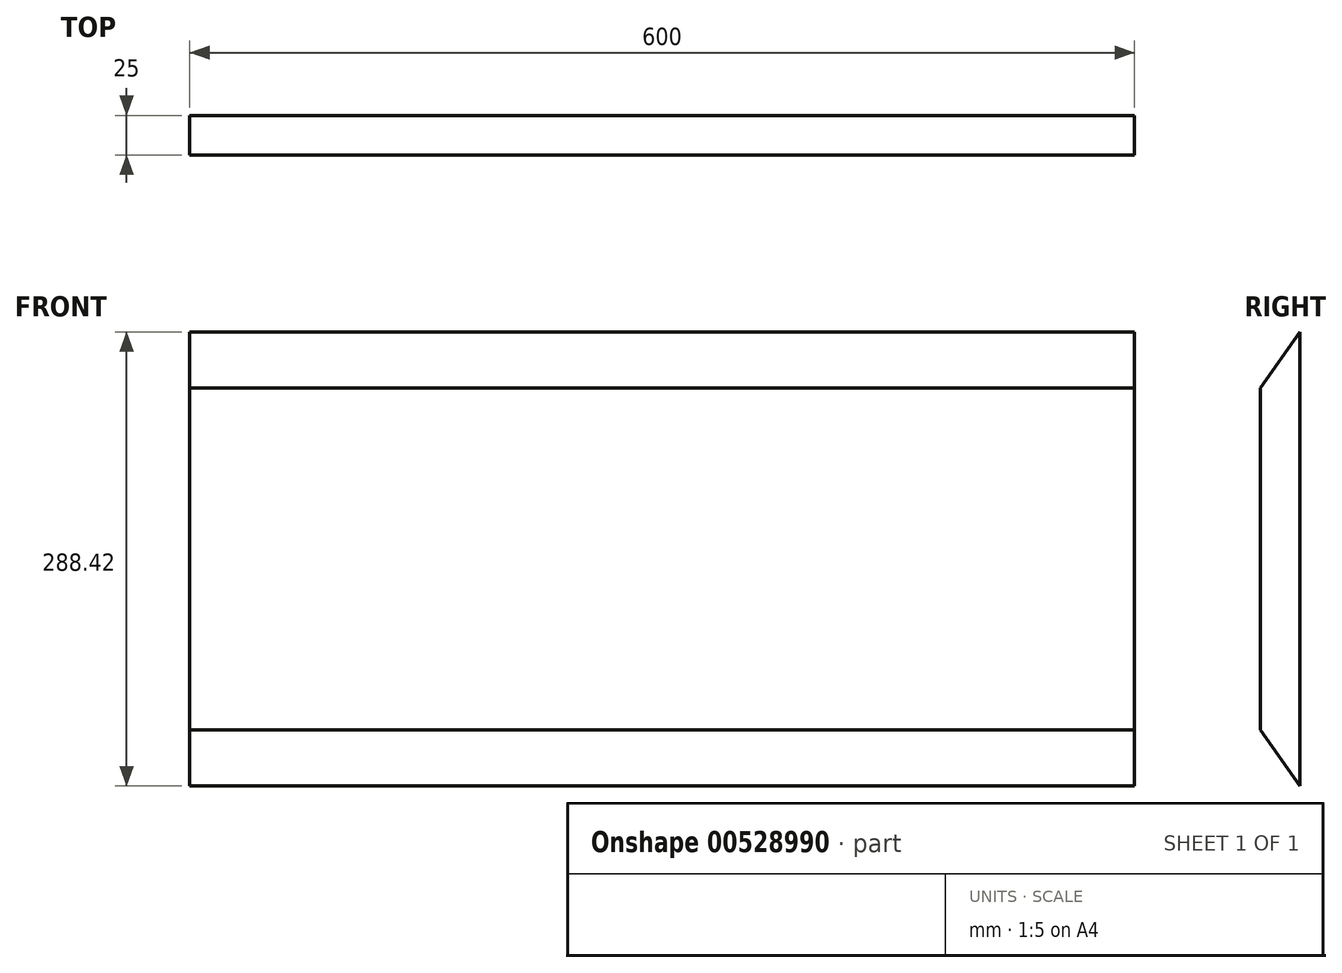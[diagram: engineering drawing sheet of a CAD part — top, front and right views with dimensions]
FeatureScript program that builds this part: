
annotation { "Feature Type Name" : "Feature", "Feature Type Description" : "" }
export const myFeature = defineFeature(function(context is Context, id is Id, definition is map)
    precondition{}
    {
        {
            var Q0;
            Q0=qCreatedBy(makeId("Right.planeOp"),FACE);
            var sketch = newSketch(context, id + "F0", { "sketchPlane" : qUnion([Q0])});
            skLineSegment(sketch, "E0", {"start": v(0, 84.61) * mm, "end": v(0, -203.8) * mm});
            skLineSegment(sketch, "E1", {"start": v(0, -203.8) * mm, "end": v(-25, -168.1) * mm});
            skLineSegment(sketch, "E2", {"start": v(-25, -168.1) * mm, "end": v(-25, 48.9) * mm});
            skLineSegment(sketch, "E3", {"start": v(-25, 48.9) * mm, "end": v(0, 84.61) * mm});
            skSolve(sketch);
        }
        {
            var Q0;
            Q0 = qSketchRegion(id + "F0", true);
            extrude(context, id + "F1", {"entities" : qUnion([Q0]), "depth" : 600 * mm, "offsetDistance" : 25.4 * mm});
        }
    });
